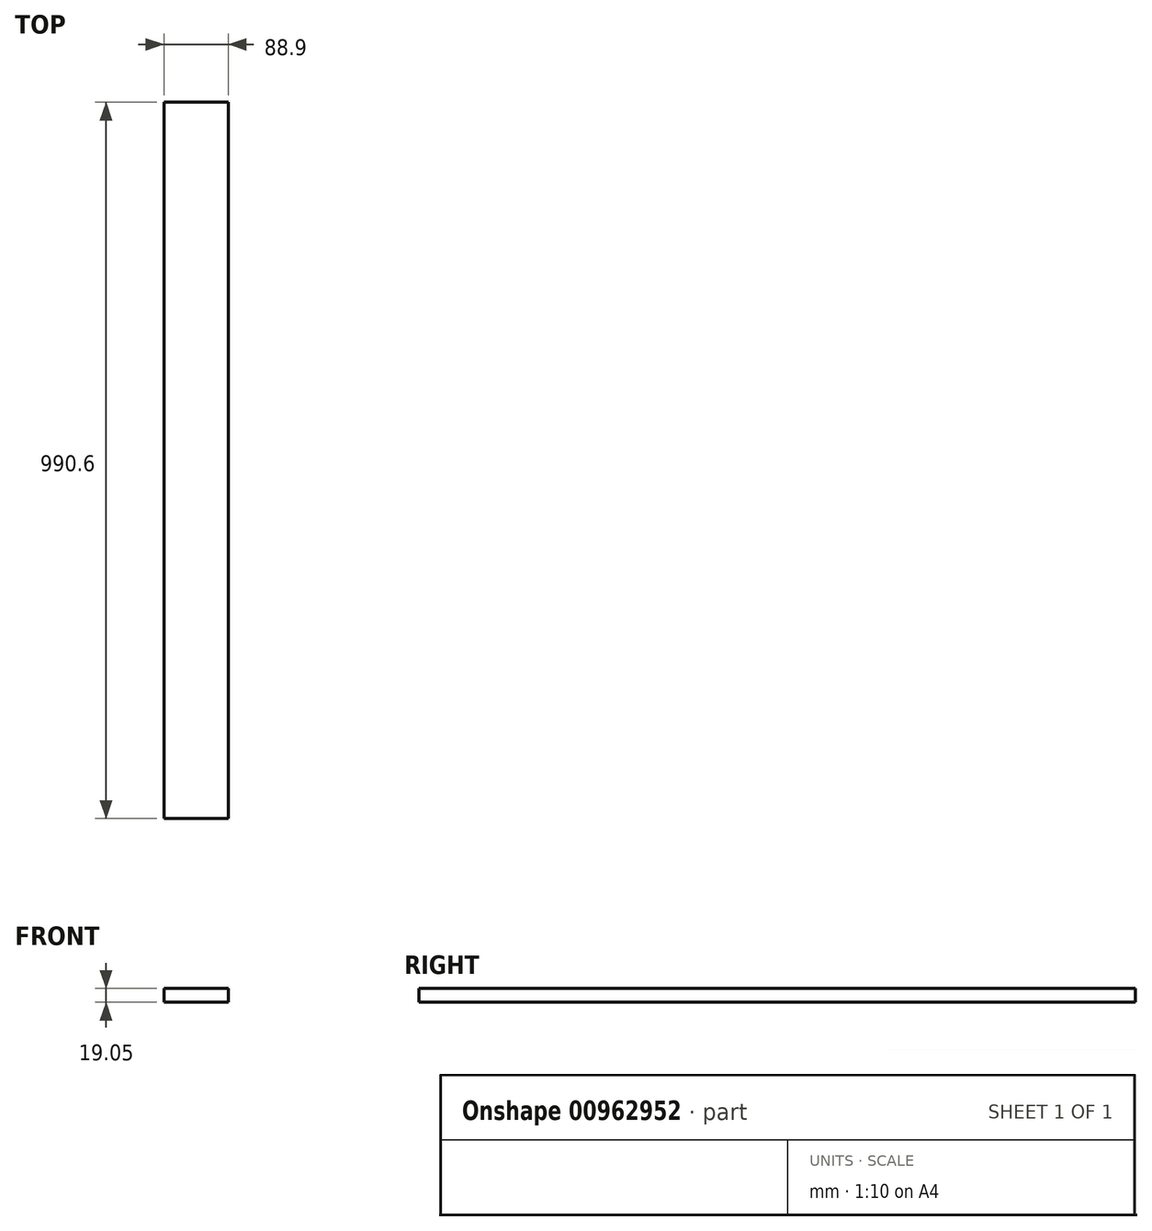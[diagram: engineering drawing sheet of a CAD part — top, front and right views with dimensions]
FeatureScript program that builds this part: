
annotation { "Feature Type Name" : "Feature", "Feature Type Description" : "" }
export const myFeature = defineFeature(function(context is Context, id is Id, definition is map)
    precondition{}
    {
        {
            var Q0;
            Q0=qCreatedBy(makeId("Front.planeOp"),FACE);
            var sketch = newSketch(context, id + "F0", { "sketchPlane" : qUnion([Q0])});
            skLineSegment(sketch, "E0.bottom", {"start": v(-7.7, 38.09) * mm, "end": v(81.2, 38.09) * mm});
            skLineSegment(sketch, "E0.top", {"start": v(-7.7, 19.04) * mm, "end": v(81.2, 19.04) * mm});
            skLineSegment(sketch, "E0.left", {"start": v(-7.7, 38.09) * mm, "end": v(-7.7, 19.04) * mm});
            skLineSegment(sketch, "E0.right", {"start": v(81.2, 38.09) * mm, "end": v(81.2, 19.04) * mm});
            skSolve(sketch);
        }
        {
            var Q0;
            Q0=makeQuery(id+"F0.imprint","IMPRINT",FACE,{"disambiguationData":[TD([[makeQuery(id+"F0.imprint","IMPRINT",EDGE,{"derivedFrom":sQuery(id+"F0.wireOp",EDGE,"E0.bottom")}),-1.0]])]});
            extrude(context, id + "F1", {"entities" : qUnion([Q0]), "depth" : 990.6 * mm, "offsetDistance" : 25.4 * mm});
        }
    });
